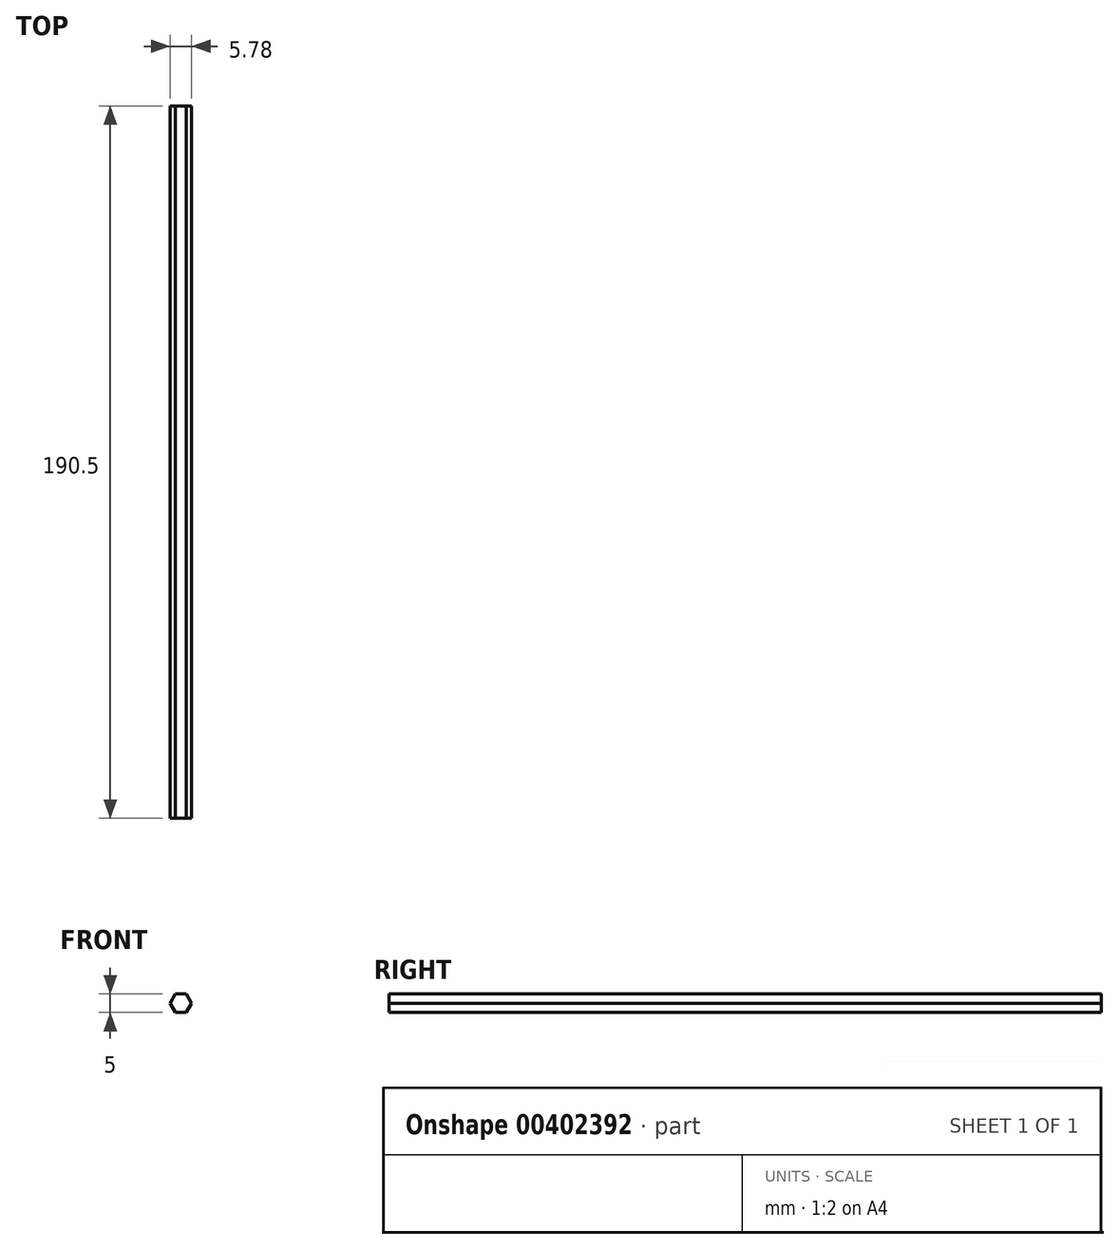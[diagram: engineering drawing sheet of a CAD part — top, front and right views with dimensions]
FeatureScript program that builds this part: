
annotation { "Feature Type Name" : "Feature", "Feature Type Description" : "" }
export const myFeature = defineFeature(function(context is Context, id is Id, definition is map)
    precondition{}
    {
        {
            var Q0;
            Q0=qCreatedBy(makeId("Front.planeOp"),FACE);
            var sketch = newSketch(context, id + "F0", { "sketchPlane" : qUnion([Q0])});
            skCircle(sketch, "E0.cCircle", {"center": v(0, 0) * mm, "radius": 2.5 * mm, "construction": true});
            skLineSegment(sketch, "E0.0", {"start": v(1.44, -2.5) * mm, "end": v(-1.44, -2.5) * mm});
            skLineSegment(sketch, "E0.1", {"start": v(-1.44, -2.5) * mm, "end": v(-2.89, 0) * mm});
            skLineSegment(sketch, "E0.2", {"start": v(-2.89, 0) * mm, "end": v(-1.44, 2.5) * mm});
            skLineSegment(sketch, "E0.3", {"start": v(-1.44, 2.5) * mm, "end": v(1.44, 2.5) * mm});
            skLineSegment(sketch, "E0.4", {"start": v(1.44, 2.5) * mm, "end": v(2.89, 0) * mm});
            skLineSegment(sketch, "E0.5", {"start": v(2.89, 0) * mm, "end": v(1.44, -2.5) * mm});
            skPoint(sketch, "E0.0.midPoint", {"position": v(0, -2.5) * mm});
            skSolve(sketch);
        }
        {
            var Q0;
            Q0=makeQuery(id+"F0.imprint","IMPRINT",FACE,{"disambiguationData":[TD([[makeQuery(id+"F0.imprint","IMPRINT",EDGE,{"derivedFrom":sQuery(id+"F0.wireOp",EDGE,"E0.0")}),-1.0]])]});
            extrude(context, id + "F1", {"entities" : qUnion([Q0]), "depth" : 190.5 * mm});
        }
    });
